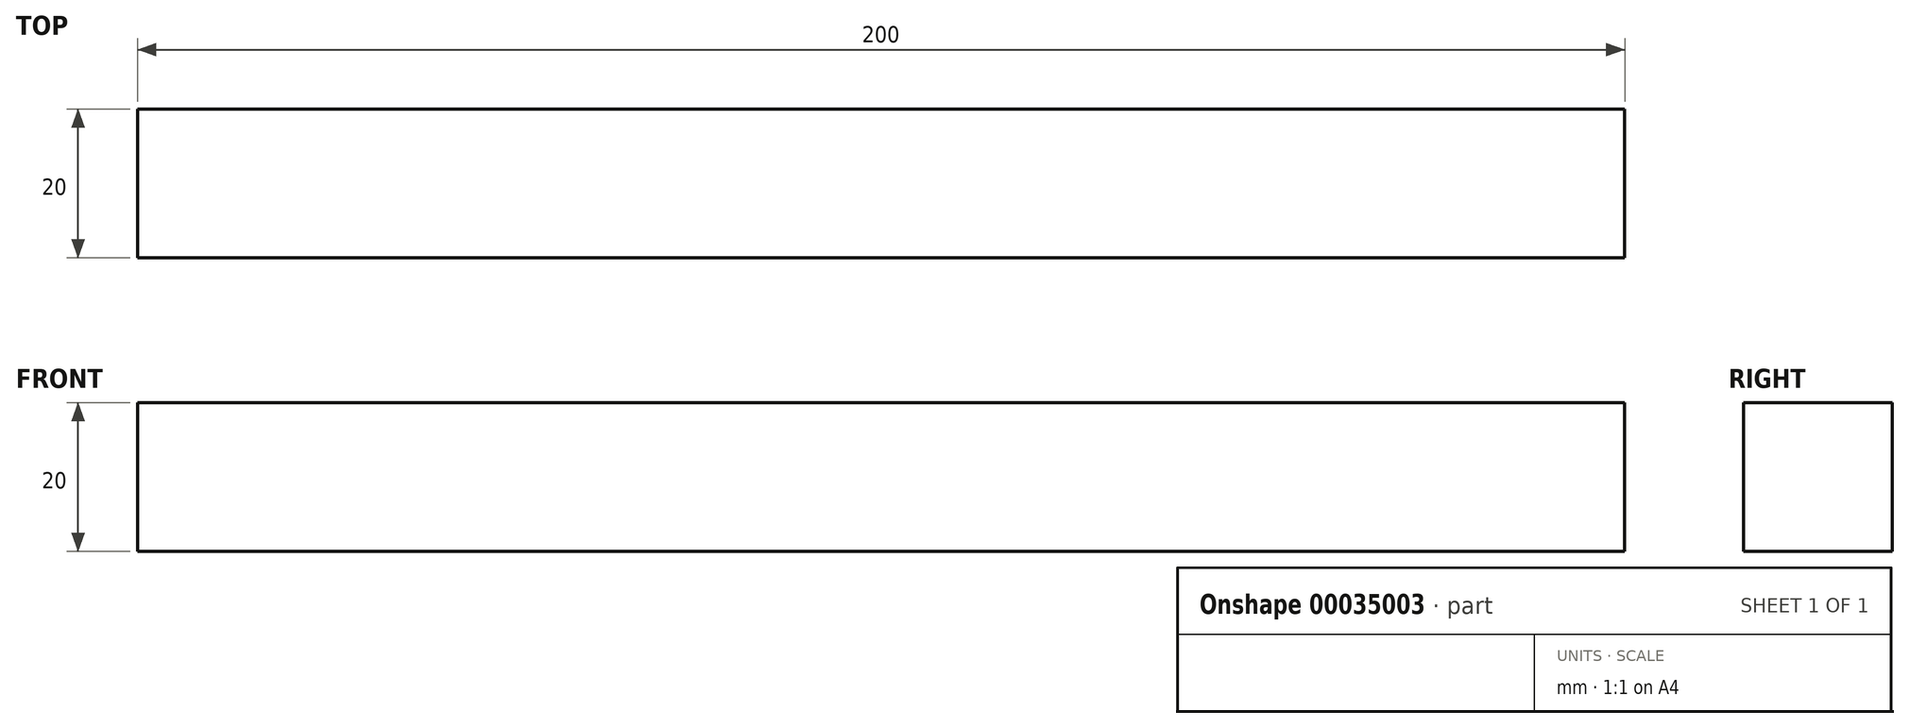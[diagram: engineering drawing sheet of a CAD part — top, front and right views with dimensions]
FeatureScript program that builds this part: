
annotation { "Feature Type Name" : "Feature", "Feature Type Description" : "" }
export const myFeature = defineFeature(function(context is Context, id is Id, definition is map)
    precondition{}
    {
        {
            var Q0;
            Q0=qCreatedBy(makeId("Top.planeOp"),FACE);
            var sketch = newSketch(context, id + "F0", { "sketchPlane" : qUnion([Q0])});
            skLineSegment(sketch, "E0.bottom", {"start": v(-97.02, -14.1) * mm, "end": v(102.98, -14.1) * mm});
            skLineSegment(sketch, "E0.top", {"start": v(-97.02, -34.1) * mm, "end": v(102.98, -34.1) * mm});
            skLineSegment(sketch, "E0.left", {"start": v(-97.02, -14.1) * mm, "end": v(-97.02, -34.1) * mm});
            skLineSegment(sketch, "E0.right", {"start": v(102.98, -14.1) * mm, "end": v(102.98, -34.1) * mm});
            skSolve(sketch);
        }
        {
            var Q0;
            Q0=makeQuery(id+"F0.imprint","IMPRINT",FACE,{"disambiguationData":[TD([[makeQuery(id+"F0.imprint","IMPRINT",EDGE,{"derivedFrom":sQuery(id+"F0.wireOp",EDGE,"E0.bottom")}),-1.0]])]});
            extrude(context, id + "F1", {"entities" : qUnion([Q0]), "depth" : 20 * mm});
        }
    });
